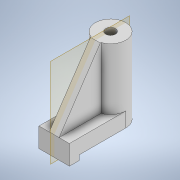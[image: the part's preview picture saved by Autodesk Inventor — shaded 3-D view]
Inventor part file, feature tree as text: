
AUTODESK INVENTOR PART (.ipt)
format: ipt  version: 2022 (Build 260153000, 153)  size: 135,680 bytes
history: native  units: mm
features: extrude x4, sketch x4, plane x1
ambient origin geometry x8: Origin, YZ Plane, XZ Plane, XY Plane, X Axis, Y Axis, Z Axis, Center Point
bodies: Solid1 (feature_tree)
feature tree (9):
  extrude  "Extrusion1"  Depth=9.5mm
  extrude  "Extrusion2"  Depth=3.0mm TaperAngle=0.0deg
  extrude  "Extrusion3"  Depth=2.0mm
  plane  "Work Plane1"
  extrude  "Extrusion4"  Depth=2.0mm TaperAngle=0.0deg
  sketch  "Sketch1"  dims[d2=6.2mm d3=9.5mm]
  sketch  "Sketch2"  dims[d4=2.0mm d5=3.0mm d6=0.0mm]
  sketch  "Sketch3"  dims[d7=12.5mm d8=0.0mm d9=2.0mm]
  sketch  "Sketch4"  dims[d10=4.0mm d11=0.0mm d12=2.0mm d13=0.0mm]
